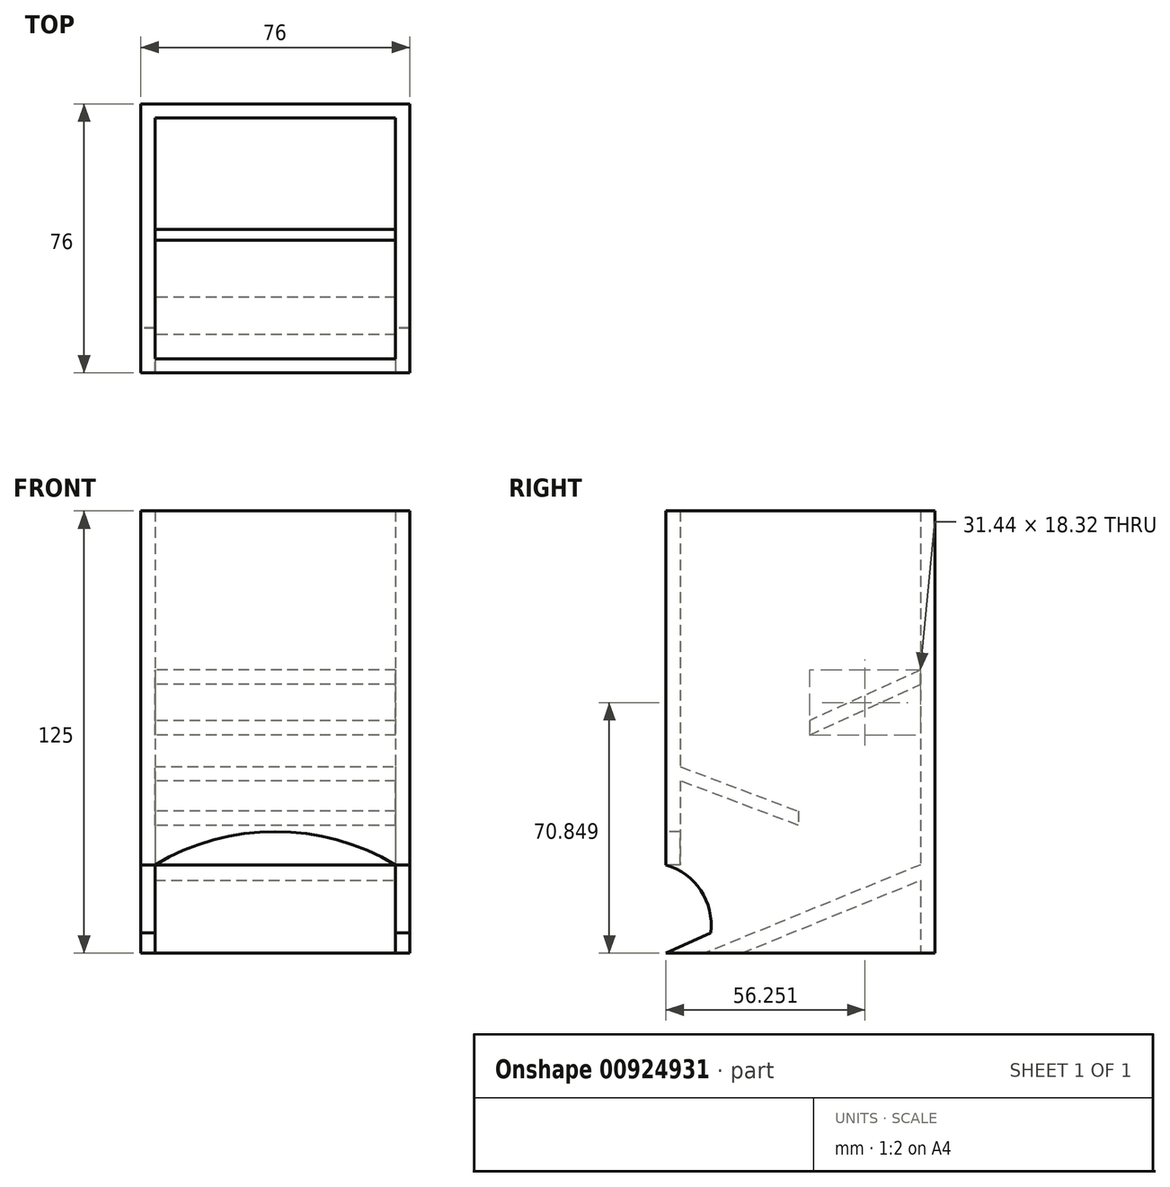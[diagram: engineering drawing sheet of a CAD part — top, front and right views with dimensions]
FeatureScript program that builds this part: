
annotation { "Feature Type Name" : "Feature", "Feature Type Description" : "" }
export const myFeature = defineFeature(function(context is Context, id is Id, definition is map)
    precondition{}
    {
        {
            var Q0;
            Q0=qCreatedBy(makeId("Top.planeOp"),FACE);
            var sketch = newSketch(context, id + "F0", { "sketchPlane" : qUnion([Q0])});
            skLineSegment(sketch, "E0.bottom", {"start": v(0, 0) * mm, "end": v(-76, 0) * mm});
            skLineSegment(sketch, "E0.top", {"start": v(0, 76) * mm, "end": v(-76, 76) * mm});
            skLineSegment(sketch, "E0.left", {"start": v(0, 0) * mm, "end": v(0, 76) * mm});
            skLineSegment(sketch, "E0.right", {"start": v(-76, 0) * mm, "end": v(-76, 76) * mm});
            skLineSegment(sketch, "E1.bottom", {"start": v(-72, 72) * mm, "end": v(-4, 72) * mm});
            skLineSegment(sketch, "E1.top", {"start": v(-72, 4) * mm, "end": v(-4, 4) * mm});
            skLineSegment(sketch, "E1.left", {"start": v(-72, 72) * mm, "end": v(-72, 4) * mm});
            skLineSegment(sketch, "E1.right", {"start": v(-4, 72) * mm, "end": v(-4, 4) * mm});
            skSolve(sketch);
        }
        {
            var Q0;
            Q0 = qSketchRegion(id + "F0", true);
            extrude(context, id + "F1", {"entities" : qUnion([Q0]), "depth" : 100 * mm, "offsetDistance" : 25 * mm});
        }
        {
            var Q0;
            Q0=makeQuery(id+"F0.imprint","IMPRINT",FACE,{"disambiguationData":[TD([[makeQuery(id+"F0.imprint","IMPRINT",EDGE,{"derivedFrom":sQuery(id+"F0.wireOp",EDGE,"E1.bottom")}),-1.0]])]});
            var sketch = newSketch(context, id + "F2", { "sketchPlane" : qUnion([Q0])});
            skLineSegment(sketch, "E2.bottom", {"start": v(-76, 0) * mm, "end": v(-72, 0) * mm});
            skLineSegment(sketch, "E2.top", {"start": v(-76, 76) * mm, "end": v(-72, 76) * mm});
            skLineSegment(sketch, "E2.left", {"start": v(-76, 0) * mm, "end": v(-76, 76) * mm});
            skLineSegment(sketch, "E2.right", {"start": v(-72, 0) * mm, "end": v(-72, 76) * mm});
            skLineSegment(sketch, "E3.bottom", {"start": v(0, 0) * mm, "end": v(-4, 0) * mm});
            skLineSegment(sketch, "E3.top", {"start": v(0, 76) * mm, "end": v(-4, 76) * mm});
            skLineSegment(sketch, "E3.left", {"start": v(0, 0) * mm, "end": v(0, 76) * mm});
            skLineSegment(sketch, "E3.right", {"start": v(-4, 0) * mm, "end": v(-4, 76) * mm});
            skLineSegment(sketch, "E4.bottom", {"start": v(-72, 76) * mm, "end": v(-4, 76) * mm});
            skLineSegment(sketch, "E4.top", {"start": v(-72, 72) * mm, "end": v(-4, 72) * mm});
            skLineSegment(sketch, "E4.left", {"start": v(-72, 76) * mm, "end": v(-72, 72) * mm});
            skLineSegment(sketch, "E4.right", {"start": v(-4, 76) * mm, "end": v(-4, 72) * mm});
            skSolve(sketch);
        }
        {
            var Q0;
            Q0 = qSketchRegion(id + "F2", true);
            extrude(context, id + "F3", {"entities" : qUnion([Q0]), "operationType" : NewBodyOperationType.ADD, "oppositeDirection" : true, "depth" : 25 * mm, "offsetDistance" : 25 * mm});
        }
        {
            var Q0;
            Q0=makeQuery(id+"F3.boolean.opBoolean","MERGE",FACE,{"derivedFrom":[makeQuery(id+"F1.opExtrude","SWEPT_FACE",FACE,{"disambiguationData":[OSD([sQuery(id+"F0.wireOp",EDGE,"E0.right")])]}),makeQuery(id+"F3.opExtrude","SWEPT_FACE",FACE,{"disambiguationData":[OSD([sQuery(id+"F2.wireOp",EDGE,"E2.left")])]})]});
            var sketch = newSketch(context, id + "F4", { "sketchPlane" : qUnion([Q0])});
            skLineSegment(sketch, "E5", {"start": v(-71.97, 0) * mm, "end": v(-10.85, -25) * mm});
            skLineSegment(sketch, "E6", {"start": v(-10.85, -25) * mm, "end": v(-21.38, -25) * mm});
            skLineSegment(sketch, "E7", {"start": v(-21.38, -25) * mm, "end": v(-76, -2.73) * mm});
            skLineSegment(sketch, "E8", {"start": v(-76, -2.73) * mm, "end": v(-76, 0) * mm});
            skLineSegment(sketch, "E9", {"start": v(-76, 0) * mm, "end": v(-71.97, 0) * mm});
            skLineSegment(sketch, "E10", {"start": v(-21.38, -25) * mm, "end": v(-10.85, -25) * mm});
            skSolve(sketch);
        }
        {
            var Q0;
            Q0 = qSketchRegion(id + "F4", true);
            var Q1;
            Q1=makeQuery(id+"F3.boolean.opBoolean","MERGE",FACE,{"derivedFrom":[makeQuery(id+"F1.opExtrude","SWEPT_FACE",FACE,{"disambiguationData":[OSD([sQuery(id+"F0.wireOp",EDGE,"E1.right")])]}),makeQuery(id+"F3.opExtrude","SWEPT_FACE",FACE,{"disambiguationData":[OSD([sQuery(id+"F2.wireOp",EDGE,"E3.right")])]})]});
            extrude(context, id + "F5", {"entities" : qUnion([Q0]), "operationType" : NewBodyOperationType.ADD, "endBound" : BoundingType.UP_TO_SURFACE, "oppositeDirection" : true, "depth" : 25 * mm, "endBoundEntityFace" : qUnion([Q1]), "offsetDistance" : 25 * mm});
        }
        {
            var Q0;
            {var subQ5=sQuery(id+"F4.wireOp",EDGE,"E5");Q0=makeQuery(id+"F4.imprint","IMPRINT",FACE,{"disambiguationData":[TD([[makeQuery(id+"F4.imprint","IMPRINT",EDGE,{"derivedFrom":subQ5}),1.0]])]});}
            var sketch = newSketch(context, id + "F6", { "sketchPlane" : qUnion([Q0])});
            skArc(sketch, "E11", {"start": v(0, 0) * mm, "mid": v(-9.85, -7.29) * mm, "end": v(-12.62, -19.22) * mm});
            skLineSegment(sketch, "E12", {"start": v(0, -25) * mm, "end": v(0, 0) * mm});
            skLineSegment(sketch, "E13", {"start": v(0, -25) * mm, "end": v(-12.62, -19.22) * mm});
            skSolve(sketch);
        }
        {
            var Q0;
            Q0 = qSketchRegion(id + "F6", true);
            var Q1;
            Q1=makeQuery(id+"F3.boolean.opBoolean","MERGE",FACE,{"derivedFrom":[makeQuery(id+"F1.opExtrude","SWEPT_FACE",FACE,{"disambiguationData":[OSD([sQuery(id+"F0.wireOp",EDGE,"E0.left")])]}),makeQuery(id+"F3.opExtrude","SWEPT_FACE",FACE,{"disambiguationData":[OSD([sQuery(id+"F2.wireOp",EDGE,"E3.left")])]})]});
            extrude(context, id + "F7", {"entities" : qUnion([Q0]), "operationType" : NewBodyOperationType.REMOVE, "endBound" : BoundingType.UP_TO_SURFACE, "oppositeDirection" : true, "depth" : 25 * mm, "endBoundEntityFace" : qUnion([Q1]), "offsetDistance" : 25 * mm});
        }
        {
            var Q0;
            Q0=makeQuery(id+"F3.boolean.opBoolean","MERGE",FACE,{"derivedFrom":[makeQuery(id+"F1.opExtrude","SWEPT_FACE",FACE,{"disambiguationData":[OSD([sQuery(id+"F0.wireOp",EDGE,"E0.bottom")])]}),makeQuery(id+"F3.opExtrude","SWEPT_FACE",FACE,{"disambiguationData":[OSD([sQuery(id+"F2.wireOp",EDGE,"E2.bottom")])]}),makeQuery(id+"F3.opExtrude","SWEPT_FACE",FACE,{"disambiguationData":[OSD([sQuery(id+"F2.wireOp",EDGE,"E3.bottom")])]})]});
            var sketch = newSketch(context, id + "F8", { "sketchPlane" : qUnion([Q0])});
            skArc(sketch, "E14", {"start": v(-4, 0) * mm, "mid": v(-38, 9.36) * mm, "end": v(-72, 0) * mm});
            skSolve(sketch);
        }
        {
            var Q0;
            Q0=makeQuery(id+"F8.imprint","IMPRINT",FACE,{"disambiguationData":[TD([[makeQuery(id+"F8.imprint","IMPRINT",EDGE,{"derivedFrom":sQuery(id+"F8.wireOp",EDGE,"E14")}),1.0]])]});
            extrude(context, id + "F9", {"entities" : qUnion([Q0]), "operationType" : NewBodyOperationType.REMOVE, "oppositeDirection" : true, "depth" : 25 * mm, "offsetDistance" : 25 * mm});
        }
        {
            var Q0;
            {var subQ5=sQuery(id+"F4.wireOp",EDGE,"E5");Q0=makeQuery(id+"F4.imprint","IMPRINT",FACE,{"disambiguationData":[TD([[makeQuery(id+"F4.imprint","IMPRINT",EDGE,{"derivedFrom":subQ5}),1.0]])]});}
            var sketch = newSketch(context, id + "F10", { "sketchPlane" : qUnion([Q0])});
            skLineSegment(sketch, "E15", {"start": v(-75.99, 0) * mm, "end": v(-66.52, 23.14) * mm, "construction": true});
            skLineSegment(sketch, "E16", {"start": v(-46.9, -12) * mm, "end": v(-37.44, 11.14) * mm, "construction": true});
            skLineSegment(sketch, "E17", {"start": v(-37.44, 11.14) * mm, "end": v(0, 25.21) * mm});
            skLineSegment(sketch, "E18", {"start": v(0, 25.21) * mm, "end": v(0, 29.21) * mm});
            skLineSegment(sketch, "E19", {"start": v(0, 29.21) * mm, "end": v(-37.44, 15.14) * mm});
            skLineSegment(sketch, "E20", {"start": v(-37.44, 15.14) * mm, "end": v(-37.44, 11.14) * mm});
            skLineSegment(sketch, "E21", {"start": v(-31.74, 17.29) * mm, "end": v(-40.53, 40.7) * mm, "construction": true});
            skLineSegment(sketch, "E22", {"start": v(-40.53, 36.7) * mm, "end": v(-71.97, 51) * mm});
            skLineSegment(sketch, "E23", {"start": v(-71.97, 51) * mm, "end": v(-71.97, 55) * mm});
            skLineSegment(sketch, "E24", {"start": v(-71.97, 55) * mm, "end": v(-40.53, 40.7) * mm});
            skLineSegment(sketch, "E25", {"start": v(-40.53, 40.7) * mm, "end": v(-40.53, 36.7) * mm});
            skSolve(sketch);
        }
        {
            var Q0;
            Q0 = qSketchRegion(id + "F10", true);
            var Q1;
            {var subQ1=sQuery(id+"F2.wireOp",EDGE,"E3.right");var subQ6=sQuery(id+"F0.wireOp",EDGE,"E0.bottom");var subQ7=sQuery(id+"F0.wireOp",EDGE,"E1.right");Q1=makeQuery(id+"F5.boolean.opBoolean","SPLIT",FACE,{"disambiguationData":[TD([makeQuery(id+"F1.opExtrude","SWEPT_FACE",FACE,{"disambiguationData":[OSD([subQ6])]})])],"derivedFrom":makeQuery(id+"F3.boolean.opBoolean","MERGE",FACE,{"derivedFrom":[makeQuery(id+"F1.opExtrude","SWEPT_FACE",FACE,{"disambiguationData":[OSD([subQ7])]}),makeQuery(id+"F3.opExtrude","SWEPT_FACE",FACE,{"disambiguationData":[OSD([subQ1])]})]})});}
            extrude(context, id + "F11", {"entities" : qUnion([Q0]), "operationType" : NewBodyOperationType.ADD, "endBound" : BoundingType.UP_TO_SURFACE, "oppositeDirection" : true, "depth" : 25 * mm, "endBoundEntityFace" : qUnion([Q1]), "offsetDistance" : 25 * mm});
        }
    });
